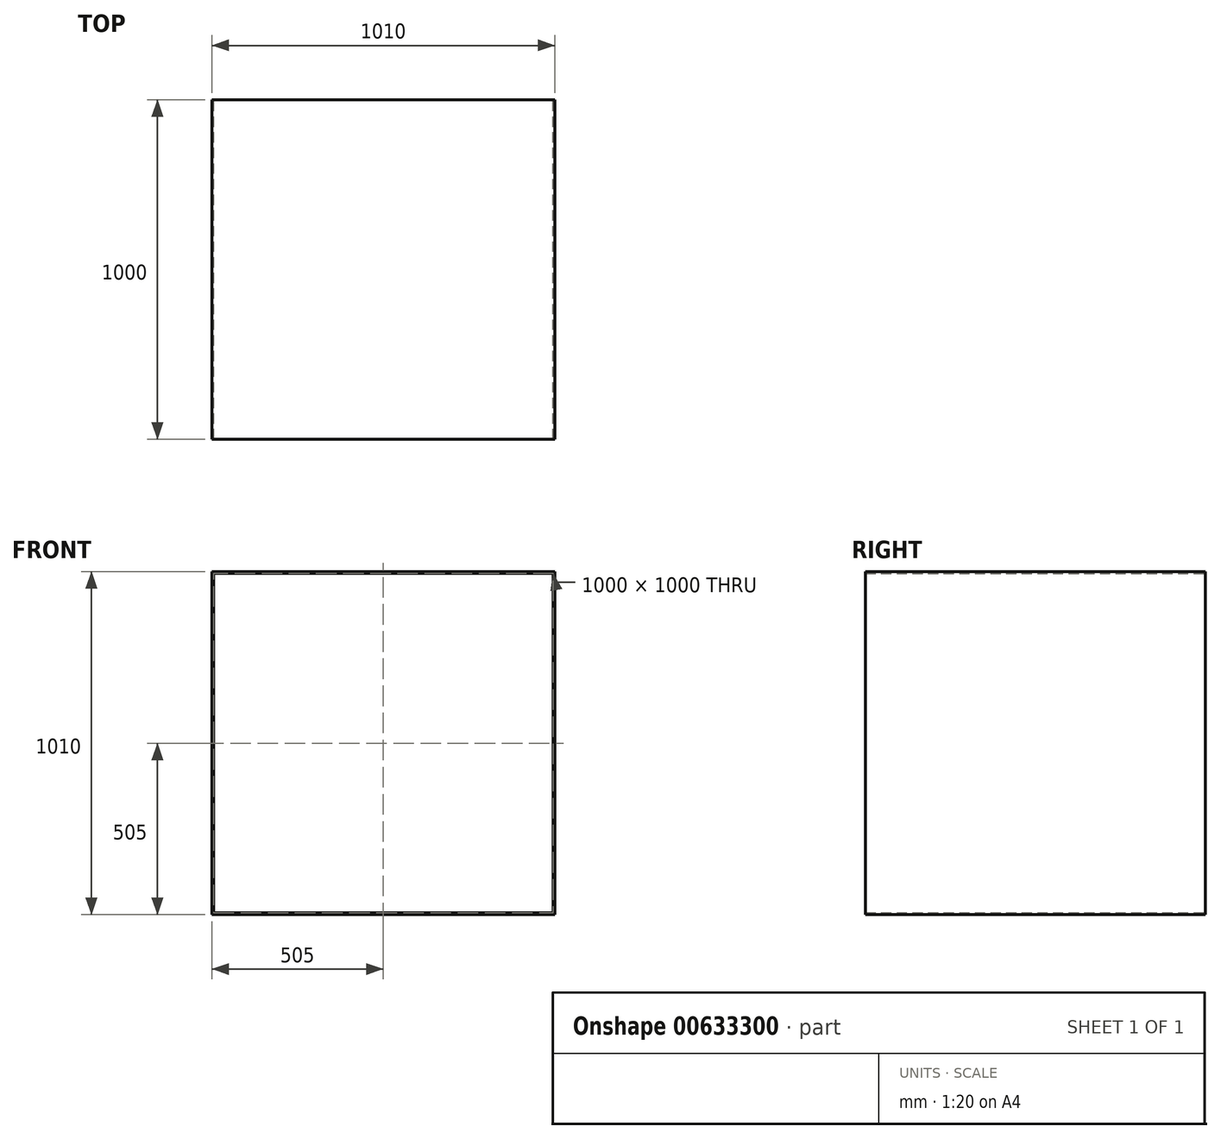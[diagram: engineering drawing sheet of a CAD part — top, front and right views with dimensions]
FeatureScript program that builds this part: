
annotation { "Feature Type Name" : "Feature", "Feature Type Description" : "" }
export const myFeature = defineFeature(function(context is Context, id is Id, definition is map)
    precondition{}
    {
        {
            var Q0;
            Q0=qCreatedBy(makeId("Front.planeOp"),FACE);
            var sketch = newSketch(context, id + "F0", { "sketchPlane" : qUnion([Q0])});
            skLineSegment(sketch, "E0.bottom", {"start": v(500, 500) * mm, "end": v(-500, 500) * mm});
            skLineSegment(sketch, "E0.top", {"start": v(500, -500) * mm, "end": v(-500, -500) * mm});
            skLineSegment(sketch, "E0.left", {"start": v(500, 500) * mm, "end": v(500, -500) * mm});
            skLineSegment(sketch, "E0.right", {"start": v(-500, 500) * mm, "end": v(-500, -500) * mm});
            skPoint(sketch, "E0.middle", {"position": v(0, 0) * mm});
            skLineSegment(sketch, "E1.bottom", {"start": v(505, 505) * mm, "end": v(-505, 505) * mm});
            skLineSegment(sketch, "E1.top", {"start": v(505, -505) * mm, "end": v(-505, -505) * mm});
            skLineSegment(sketch, "E1.left", {"start": v(505, 505) * mm, "end": v(505, -505) * mm});
            skLineSegment(sketch, "E1.right", {"start": v(-505, 505) * mm, "end": v(-505, -505) * mm});
            skSolve(sketch);
        }
        {
            var Q0;
            Q0 = qSketchRegion(id + "F0", true);
            extrude(context, id + "F1", {"entities" : qUnion([Q0]), "endBound" : BoundingType.SYMMETRIC, "depth" : 1000 * mm, "offsetDistance" : 25 * mm});
        }
    });
